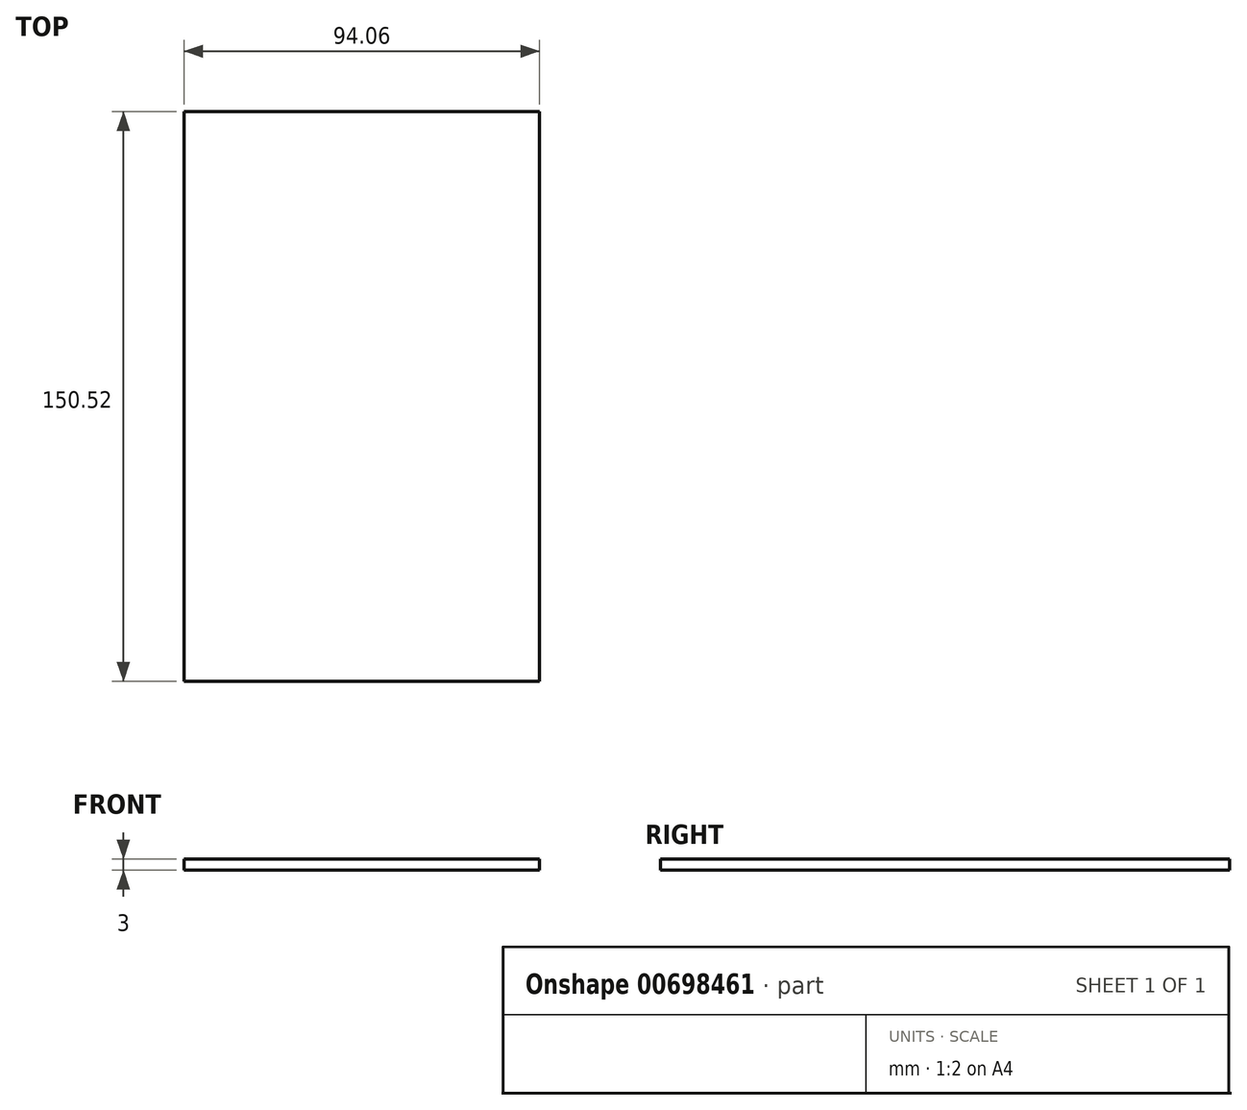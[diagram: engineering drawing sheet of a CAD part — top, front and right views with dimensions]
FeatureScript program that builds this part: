
annotation { "Feature Type Name" : "Feature", "Feature Type Description" : "" }
export const myFeature = defineFeature(function(context is Context, id is Id, definition is map)
    precondition{}
    {
        {
            var Q0;
            Q0=qCreatedBy(makeId("Top.planeOp"),FACE);
            var sketch = newSketch(context, id + "F0", { "sketchPlane" : qUnion([Q0])});
            skLineSegment(sketch, "E0.bottom", {"start": v(47.03, 75.26) * mm, "end": v(-47.03, 75.26) * mm});
            skLineSegment(sketch, "E0.top", {"start": v(47.03, -75.26) * mm, "end": v(-47.03, -75.26) * mm});
            skLineSegment(sketch, "E0.left", {"start": v(47.03, 75.26) * mm, "end": v(47.03, -75.26) * mm});
            skLineSegment(sketch, "E0.right", {"start": v(-47.03, 75.26) * mm, "end": v(-47.03, -75.26) * mm});
            skPoint(sketch, "E0.middle", {"position": v(0, 0) * mm});
            skSolve(sketch);
        }
        {
            var Q0;
            Q0 = qSketchRegion(id + "F0", true);
            extrude(context, id + "F1", {"entities" : qUnion([Q0]), "depth" : 3 * mm, "offsetDistance" : 25.4 * mm});
        }
    });
